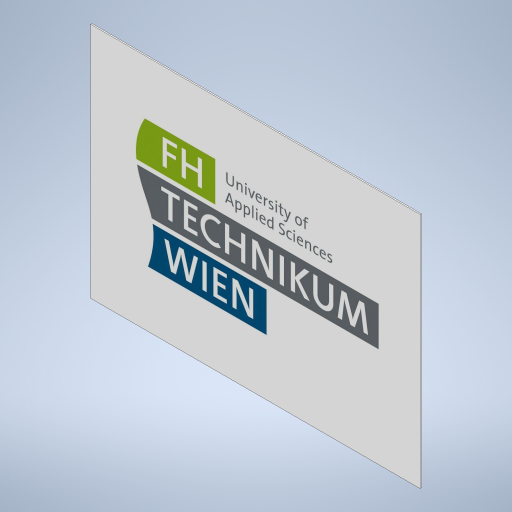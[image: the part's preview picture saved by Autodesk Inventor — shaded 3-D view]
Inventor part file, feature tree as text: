
AUTODESK INVENTOR PART (.ipt)
format: ipt  version: 2023 (Build 270158000, 158)  size: 452,608 bytes
history: native  units: mm
features: other x2, sketch x2, extrude x1, plane x1
ambient origin geometry x8: Origin, YZ Plane, XZ Plane, XY Plane, X Axis, Y Axis, Z Axis, Center Point
bodies: Solid1 (feature_tree)
feature tree (6):
  extrude  "Extrusion1"  Depth=540.0mm
  plane  "Work Plane2"
  other  "Decal1"
  sketch  "Sketch1"  dims[d0=750.0mm d1=540.0mm]
  sketch  "Sketch3"  dims[d2=3.0mm d3=0.0mm d13=0.0mm d28=0.0mm d29=750.0mm d30=750.0mm d35=540.0mm d38=750.0mm d39=105.0mm]
  other  "Image4"
